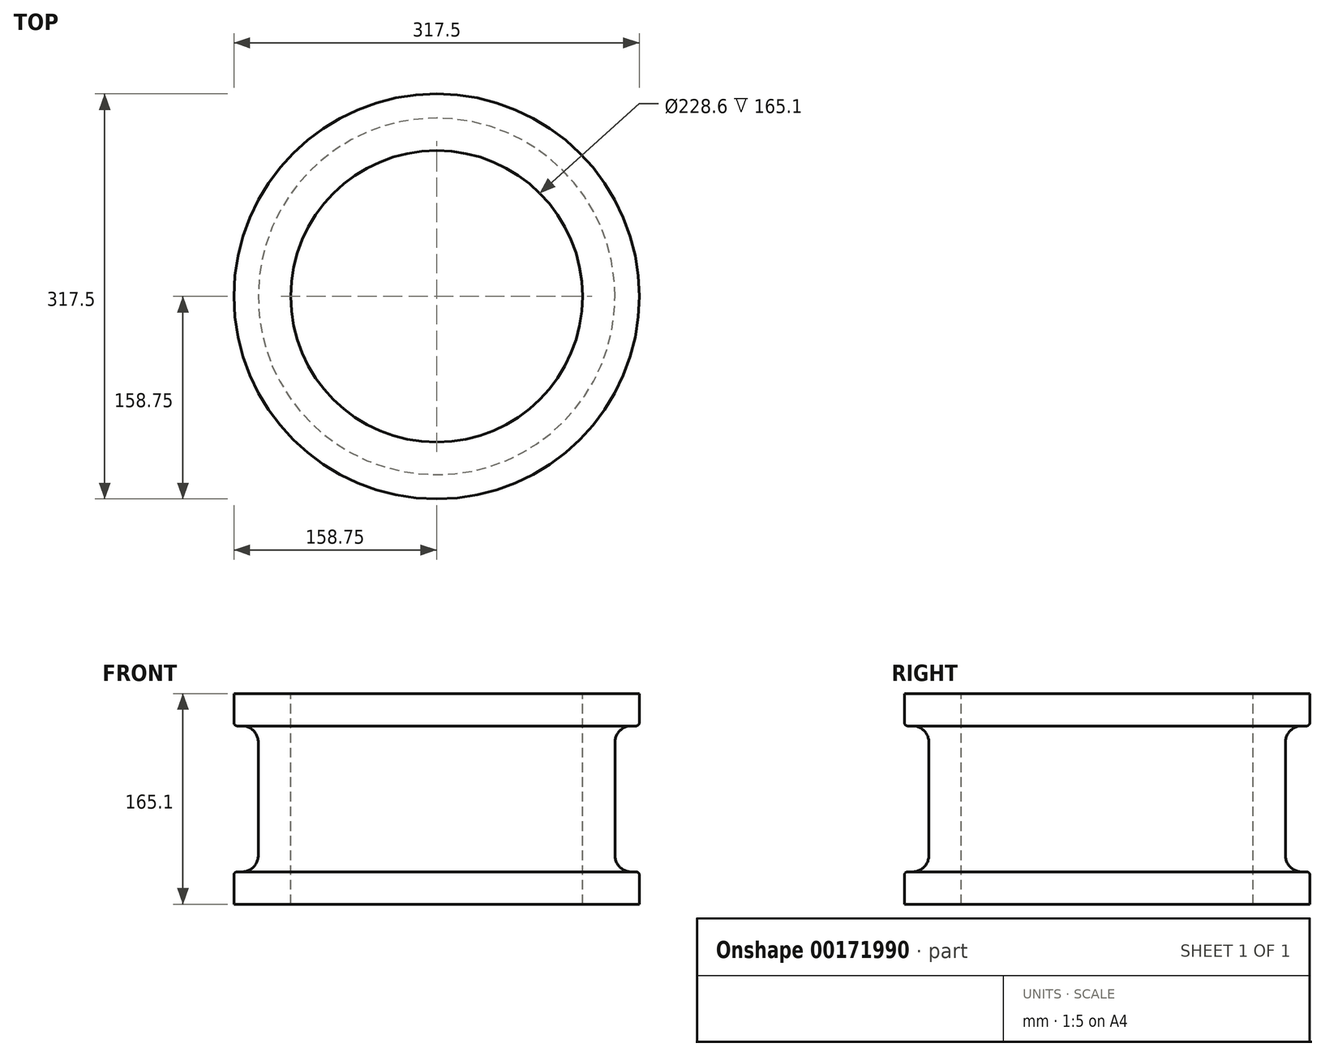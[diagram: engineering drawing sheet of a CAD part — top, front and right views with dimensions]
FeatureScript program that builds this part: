
annotation { "Feature Type Name" : "Feature", "Feature Type Description" : "" }
export const myFeature = defineFeature(function(context is Context, id is Id, definition is map)
    precondition{}
    {
        {
            var Q0;
            Q0=qCreatedBy(makeId("Front.planeOp"),FACE);
            var sketch = newSketch(context, id + "F0", { "sketchPlane" : qUnion([Q0])});
            skLineSegment(sketch, "E0", {"start": v(0, 0) * mm, "end": v(0, 165.1) * mm});
            skLineSegment(sketch, "E1", {"start": v(0, 165.1) * mm, "end": v(158.75, 165.1) * mm});
            skLineSegment(sketch, "E2", {"start": v(158.75, 165.1) * mm, "end": v(158.75, 139.7) * mm});
            skLineSegment(sketch, "E3", {"start": v(158.75, 139.7) * mm, "end": v(139.7, 139.7) * mm});
            skLineSegment(sketch, "E4", {"start": v(0, 0) * mm, "end": v(158.75, 0) * mm});
            skLineSegment(sketch, "E5", {"start": v(158.75, 0) * mm, "end": v(158.75, 25.4) * mm});
            skLineSegment(sketch, "E6", {"start": v(158.75, 25.4) * mm, "end": v(139.7, 25.4) * mm});
            skLineSegment(sketch, "E7", {"start": v(139.7, 25.4) * mm, "end": v(139.7, 139.7) * mm});
            skSolve(sketch);
        }
        {
            var Q0;
            Q0=qSketchRegion(id+"F0",true);
            var Q1;
            Q1=sQuery(id+"F0.wireOp",EDGE,"E0");
            revolve(context, id + "F1", {"entities" : qUnion([Q0]), "axis" : qUnion([Q1]), "revolveType" : RevolveType.FULL});
        }
        {
            var Q0;
            Q0=makeQuery(id+"F1.opRevolve","SWEPT_EDGE",EDGE,{"disambiguationData":[OSD([sQuery(id+"F0.wireOp",EDGE,"E3"),sQuery(id+"F0.wireOp",EDGE,"E7")])]});
            var Q1;
            Q1=makeQuery(id+"F1.opRevolve","SWEPT_EDGE",EDGE,{"disambiguationData":[OSD([sQuery(id+"F0.wireOp",EDGE,"E6"),sQuery(id+"F0.wireOp",EDGE,"E7")])]});
            fillet(context, id + "F2", {"entities" : qUnion([Q0, Q1]), "radius" : 12.7 * mm, "tangentPropagation" : true, "allowEdgeOverflow" : false});
        }
        {
            var Q0;
            Q0=makeQuery(id+"F1.opRevolve","SWEPT_EDGE",EDGE,{"disambiguationData":[OSD([sQuery(id+"F0.wireOp",EDGE,"E5"),sQuery(id+"F0.wireOp",EDGE,"E6")])]});
            var Q1;
            Q1=makeQuery(id+"F1.opRevolve","SWEPT_EDGE",EDGE,{"disambiguationData":[OSD([sQuery(id+"F0.wireOp",EDGE,"E2"),sQuery(id+"F0.wireOp",EDGE,"E3")])]});
            fillet(context, id + "F3", {"entities" : qUnion([Q0, Q1]), "radius" : 2.54 * mm, "tangentPropagation" : true, "allowEdgeOverflow" : false});
        }
        {
            var Q0;
            Q0=makeQuery(id+"F1.opRevolve","SWEPT_FACE",FACE,{"disambiguationData":[OSD([sQuery(id+"F0.wireOp",EDGE,"E1")])]});
            var sketch = newSketch(context, id + "F4", { "sketchPlane" : qUnion([Q0])});
            skCircle(sketch, "E8", {"center": v(0, 0) * mm, "radius": 114.3 * mm});
            skSolve(sketch);
        }
        {
            var Q0;
            Q0=qSketchRegion(id+"F4",true);
            extrude(context, id + "F5", {"entities" : qUnion([Q0]), "operationType" : NewBodyOperationType.REMOVE, "endBound" : BoundingType.THROUGH_ALL, "oppositeDirection" : true, "depth" : 25.4 * mm});
        }
    });
